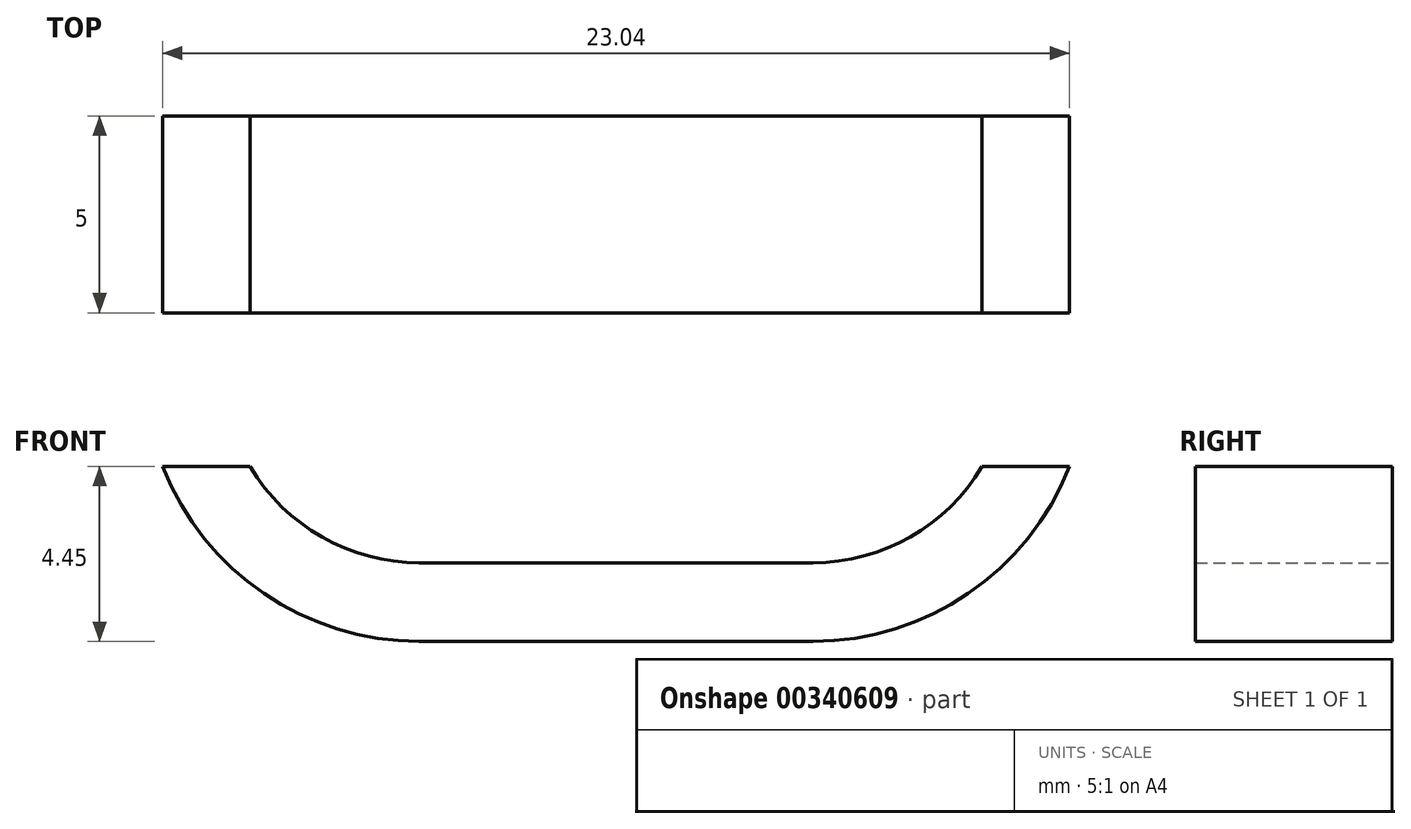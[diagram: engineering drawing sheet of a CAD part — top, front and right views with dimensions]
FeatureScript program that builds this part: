
annotation { "Feature Type Name" : "Feature", "Feature Type Description" : "" }
export const myFeature = defineFeature(function(context is Context, id is Id, definition is map)
    precondition{}
    {
        {
            var Q0;
            Q0=qCreatedBy(makeId("Front.planeOp"),FACE);
            var sketch = newSketch(context, id + "F0", { "sketchPlane" : qUnion([Q0])});
            skLineSegment(sketch, "E0", {"start": v(0, 0) * mm, "end": v(10, 0) * mm});
            skArc(sketch, "E1", {"start": v(0, 0) * mm, "mid": v(-2.47, 0.65) * mm, "end": v(-4.3, 2.45) * mm});
            skArc(sketch, "E2", {"start": v(10, 0) * mm, "mid": v(12.47, 0.65) * mm, "end": v(14.3, 2.45) * mm});
            skArc(sketch, "E3.0", {"start": v(0, -2) * mm, "mid": v(-3.94, -0.78) * mm, "end": v(-6.52, 2.45) * mm});
            skLineSegment(sketch, "E3.1", {"start": v(0, -2) * mm, "end": v(10, -2) * mm});
            skArc(sketch, "E3.2", {"start": v(10, -2) * mm, "mid": v(13.94, -0.78) * mm, "end": v(16.52, 2.45) * mm});
            skLineSegment(sketch, "E4", {"start": v(-6.52, 2.45) * mm, "end": v(-4.3, 2.45) * mm});
            skLineSegment(sketch, "E5.trimOffspring", {"start": v(14.3, 2.45) * mm, "end": v(16.52, 2.45) * mm});
            skSolve(sketch);
        }
        {
            var Q0;
            Q0=makeQuery(id+"F0.imprint","IMPRINT",FACE,{"disambiguationData":[TD([[makeQuery(id+"F0.imprint","IMPRINT",EDGE,{"derivedFrom":sQuery(id+"F0.wireOp",EDGE,"E0")}),-1.0]])]});
            extrude(context, id + "F1", {"entities" : qUnion([Q0]), "depth" : 5 * mm});
        }
    });
